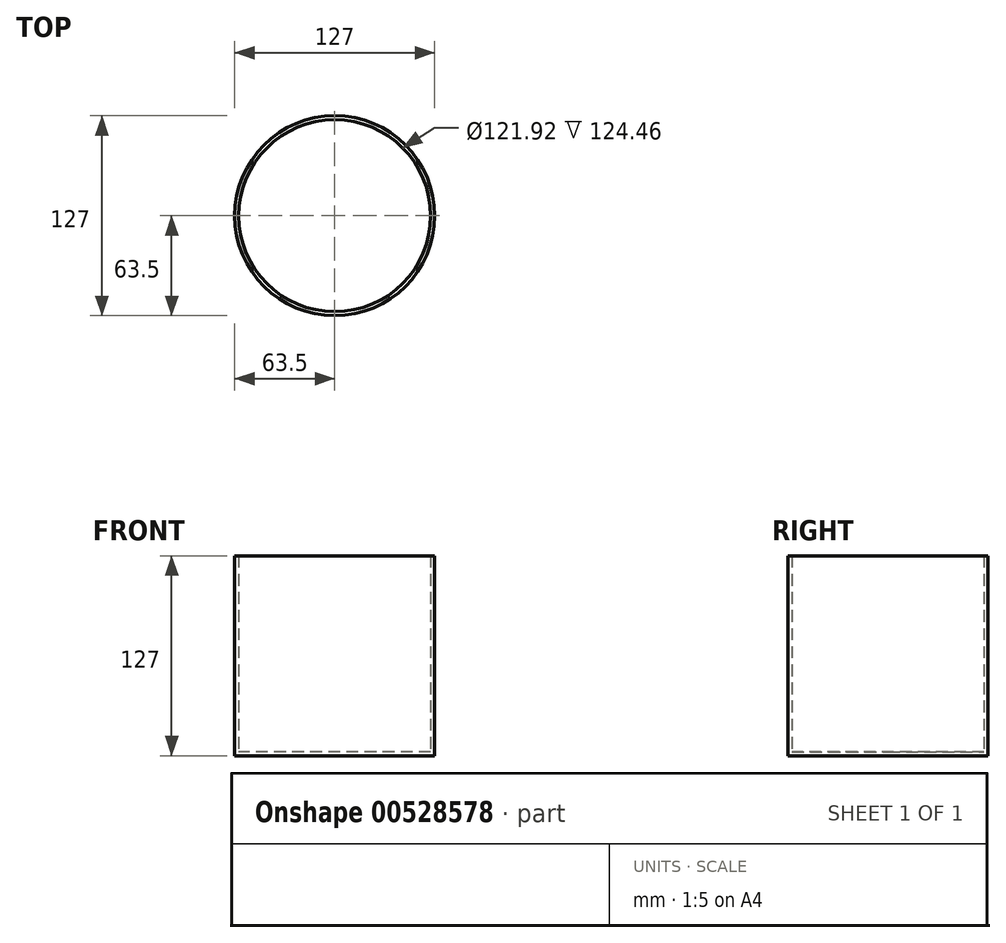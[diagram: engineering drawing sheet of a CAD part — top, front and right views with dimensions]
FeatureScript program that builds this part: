
annotation { "Feature Type Name" : "Feature", "Feature Type Description" : "" }
export const myFeature = defineFeature(function(context is Context, id is Id, definition is map)
    precondition{}
    {
        {
            var Q0;
            Q0=qCreatedBy(makeId("Top.planeOp"),FACE);
            var sketch = newSketch(context, id + "F0", { "sketchPlane" : qUnion([Q0])});
            skCircle(sketch, "E0", {"center": v(0, 0) * mm, "radius": 63.5 * mm});
            skSolve(sketch);
        }
        {
            var Q0;
            Q0 = qSketchRegion(id + "F0", true);
            extrude(context, id + "F1", {"entities" : qUnion([Q0]), "depth" : 63.5 * mm, "offsetDistance" : 25.4 * mm, "hasSecondDirection" : true, "secondDirectionOppositeDirection" : true, "secondDirectionDepth" : 63.5 * mm});
        }
        {
            var Q0;
            Q0=makeQuery(id+"F1.opExtrude","CAP_FACE",FACE,{"disambiguationData":[OSD([sQuery(id+"F0.wireOp",EDGE,"E0")])],"isStart":false});
            shell(context, id + "F2", {"entities" : qUnion([Q0]), "thickness" : 2.54 * mm});
        }
        {
            var Q0;
            Q0=qCreatedBy(makeId("Front.planeOp"),FACE);
            var sketch = newSketch(context, id + "F3", { "sketchPlane" : qUnion([Q0])});
            skLineSegment(sketch, "E1", {"start": v(63.73, 63.74) * mm, "end": v(23.4, 90.4) * mm});
            skLineSegment(sketch, "E2", {"start": v(0, 63.67) * mm, "end": v(0, 93.2) * mm});
            skSolve(sketch);
        }
        {
            var Q0;
            Q0=sQuery(id+"F3.wireOp",EDGE,"E1");
            var Q1;
            Q1=sQuery(id+"F3.wireOp",EDGE,"E2");
            revolve(context, id + "F4", {"bodyType" : ToolBodyType.SURFACE, "surfaceEntities" : qUnion([Q0]), "axis" : qUnion([Q1]), "revolveType" : RevolveType.FULL});
        }
    });
